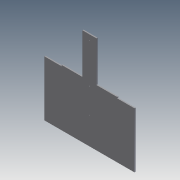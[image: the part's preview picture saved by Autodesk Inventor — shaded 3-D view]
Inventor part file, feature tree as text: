
AUTODESK INVENTOR PART (.ipt)
format: ipt  version: 2011 (Build 150239000, 239)  size: 1,121,792 bytes
history: native  units: in
note: dims shown in document units (in); Inventor stores cm internally (conversion verified against a paired STEP export)
features: extrude x38, sketch x38, fillet x1
ambient origin geometry x8: Origin, YZ Plane, XZ Plane, XY Plane, X Axis, Y Axis, Z Axis, Center Point
bodies: Solid1 (feature_tree)
feature tree (77):
  extrude  "Extrusion1"  Depth=35.0in
  extrude  "Extrusion2"  Depth=1.5in
  extrude  "Extrusion3"  Depth=0.75in
  extrude  "Extrusion4"  Depth=2.25in
  fillet  "Fillet1"  Radius=0.156in
  extrude  "Extrusion5"  Depth=0.25in TaperAngle=0.0deg
  extrude  "Extrusion6"  Depth=3.0in
  extrude  "Extrusion7"  Depth=1.0in
  extrude  "Extrusion8"  Depth=0.25in TaperAngle=0.0deg
  extrude  "Extrusion9"  Depth=3.5in
  extrude  "Extrusion10"  Depth=3.5in
  extrude  "Extrusion11"  Depth=0.25in TaperAngle=0.0deg
  extrude  "Extrusion12"  Depth=0.25in
  extrude  "Extrusion13"  Depth=1.0in
  extrude  "Extrusion14"  Depth=1.0in
  extrude  "Extrusion15"  Depth=1.0in
  extrude  "Extrusion16"  Depth=1.0in
  extrude  "Extrusion17"  Depth=1.0in
  extrude  "Extrusion18"  Depth=1.0in
  extrude  "Extrusion19"  Depth=1.0in
  extrude  "Extrusion20"  Depth=1.0in
  extrude  "Extrusion21"  Depth=1.0in
  extrude  "Extrusion22"  Depth=1.0in
  extrude  "Extrusion23"  Depth=2.0in
  extrude  "Extrusion24"  Depth=2.0in
  extrude  "Extrusion25"  Depth=2.0in
  extrude  "Extrusion26"  Depth=2.0in
  extrude  "Extrusion27"  Depth=2.0in
  extrude  "Extrusion28"  Depth=2.0in
  extrude  "Extrusion29"  Depth=2.0in
  extrude  "Extrusion30"  Depth=2.0in
  extrude  "Extrusion31"  Depth=2.0in
  extrude  "Extrusion32"  Depth=0.25in TaperAngle=0.0deg
  extrude  "Extrusion33"  Depth=0.75in
  extrude  "Extrusion34"  Depth=0.75in
  extrude  "Extrusion35"  Depth=2.0in
  extrude  "Extrusion36"  Depth=2.0in
  extrude  "Extrusion37"  Depth=2.0in
  extrude  "Extrusion38"  Depth=2.0in
  sketch  "Sketch1"  dims[d0=19.5in d1=35.0in]
  sketch  "Sketch2"  dims[d2=0.25in d3=0.0in d4=1.5in]
  sketch  "Sketch3"  dims[d5=3.0in d6=0.75in]
  sketch  "Sketch4"  dims[d7=0.75in d8=2.25in d9=0.156in]
  sketch  "Sketch5"  dims[d10=0.156in d11=0.25in d12=0.0in]
  sketch  "Sketch6"  dims[d13=1.5in d14=3.0in]
  sketch  "Sketch7"  dims[d15=1.5in d16=1.0in]
  sketch  "Sketch8"  dims[d17=32.25in d18=0.25in d19=0.0in]
  sketch  "Sketch9"  dims[d20=2.0in d21=3.5in]
  sketch  "Sketch10"  dims[d22=2.0in d23=3.5in]
  sketch  "Sketch11"  dims[d24=1.5in d25=0.25in d26=0.0in]
  sketch  "Sketch12"  dims[d27=0.25in d28=0.25in]
  sketch  "Sketch13"  dims[d29=0.25in d30=1.0in]
  sketch  "Sketch14"  dims[d31=1.0in d32=1.0in]
  sketch  "Sketch15"  dims[d33=1.0in d34=1.0in]
  sketch  "Sketch16"  dims[d35=1.0in d36=1.0in]
  sketch  "Sketch17"  dims[d37=1.0in d38=1.0in]
  sketch  "Sketch18"  dims[d39=1.0in d40=1.0in]
  sketch  "Sketch19"  dims[d41=1.0in d42=1.0in]
  sketch  "Sketch20"  dims[d43=1.0in d44=1.0in]
  sketch  "Sketch21"  dims[d45=1.0in d46=1.0in]
  sketch  "Sketch22"  dims[d47=1.0in d48=1.0in]
  sketch  "Sketch23"  dims[d49=0.25in d50=0.0in d51=2.0in]
  sketch  "Sketch24"  dims[d52=2.0in d53=2.0in]
  sketch  "Sketch25"  dims[d54=2.0in d55=2.0in]
  sketch  "Sketch26"  dims[d56=2.0in d57=2.0in]
  sketch  "Sketch27"  dims[d58=2.0in d59=2.0in]
  sketch  "Sketch28"  dims[d60=2.0in d61=2.0in]
  sketch  "Sketch29"  dims[d62=2.0in d63=2.0in]
  sketch  "Sketch30"  dims[d64=2.0in d65=2.0in]
  sketch  "Sketch31"  dims[d66=2.0in d67=2.0in]
  sketch  "Sketch32"  dims[d68=0.25in d69=0.0in d70=0.25in d71=0.0in]
  sketch  "Sketch33"  dims[d72=0.25in d73=0.0in d74=0.75in]
  sketch  "Sketch34"  dims[d75=0.25in d76=0.75in]
  sketch  "Sketch35"  dims[d77=0.25in d78=2.0in]
  sketch  "Sketch36"  dims[d79=2.0in d80=2.0in]
  sketch  "Sketch37"  dims[d81=2.0in d82=2.0in]
  sketch  "Sketch38"  dims[d83=2.0in d84=2.0in d85=2.0in d86=0.25in d87=0.0in d88=2.0in d89=2.0in d90=2.0in d91=2.0in d92=0.25in d93=0.0in d94=2.0in d95=2.0in d96=0.25in d97=0.0in d98=0.25in d99=0.25in d100=0.0in d101=9.0in d102=0.5in d103=0.75in d104=1.0in d105=0.0in d106=1.0in d107=0.0in d108=9.25in d109=0.25in d110=2.0in d111=0.25in d112=2.0in d113=4.0in d114=2.0in d115=1.0in d116=0.0in d117=0.25in d118=0.0in d119=0.25in d120=0.0in d121=0.5in d122=2.5in d123=0.5in d124=2.5in d125=0.156in d126=0.156in d127=0.25in d128=0.0in d129=0.25in d130=1.0in d131=0.0in d134=2.49in d135=8.0in d136=16.5in d137=0.185in d138=0.0925in d139=1.0in d140=0.0in d141=0.7in d142=1.0in d143=0.0in d144=1.0in d145=0.0in d146=0.25in d147=0.0in d148=0.25in d149=0.0in d150=5.853in d151=0.363in d152=0.363in d153=0.25in d154=0.0in d155=0.25in d156=0.0in d157=0.25in d158=0.0in d159=0.25in d160=0.0in d161=0.25in d162=0.0in d163=12.499in d164=1.0in d165=0.0in d166=1.5in d167=3.0in d168=8.5in d169=0.25in d170=0.0in d171=8.593in d172=0.25in d173=0.0in d174=0.25in d175=1.0in d176=0.0in d177=3.5in d178=0.25in d179=3.5in d180=0.25in d181=1.0in d182=0.0in d183=0.25in d184=0.0in d185=0.25in d186=0.0in d187=3.75in d188=0.25in d189=3.75in d190=0.25in d191=1.0in d192=0.0in d193=1.0in d194=2.0in d195=1.0in d196=2.0in d197=0.25in d198=0.0in]
